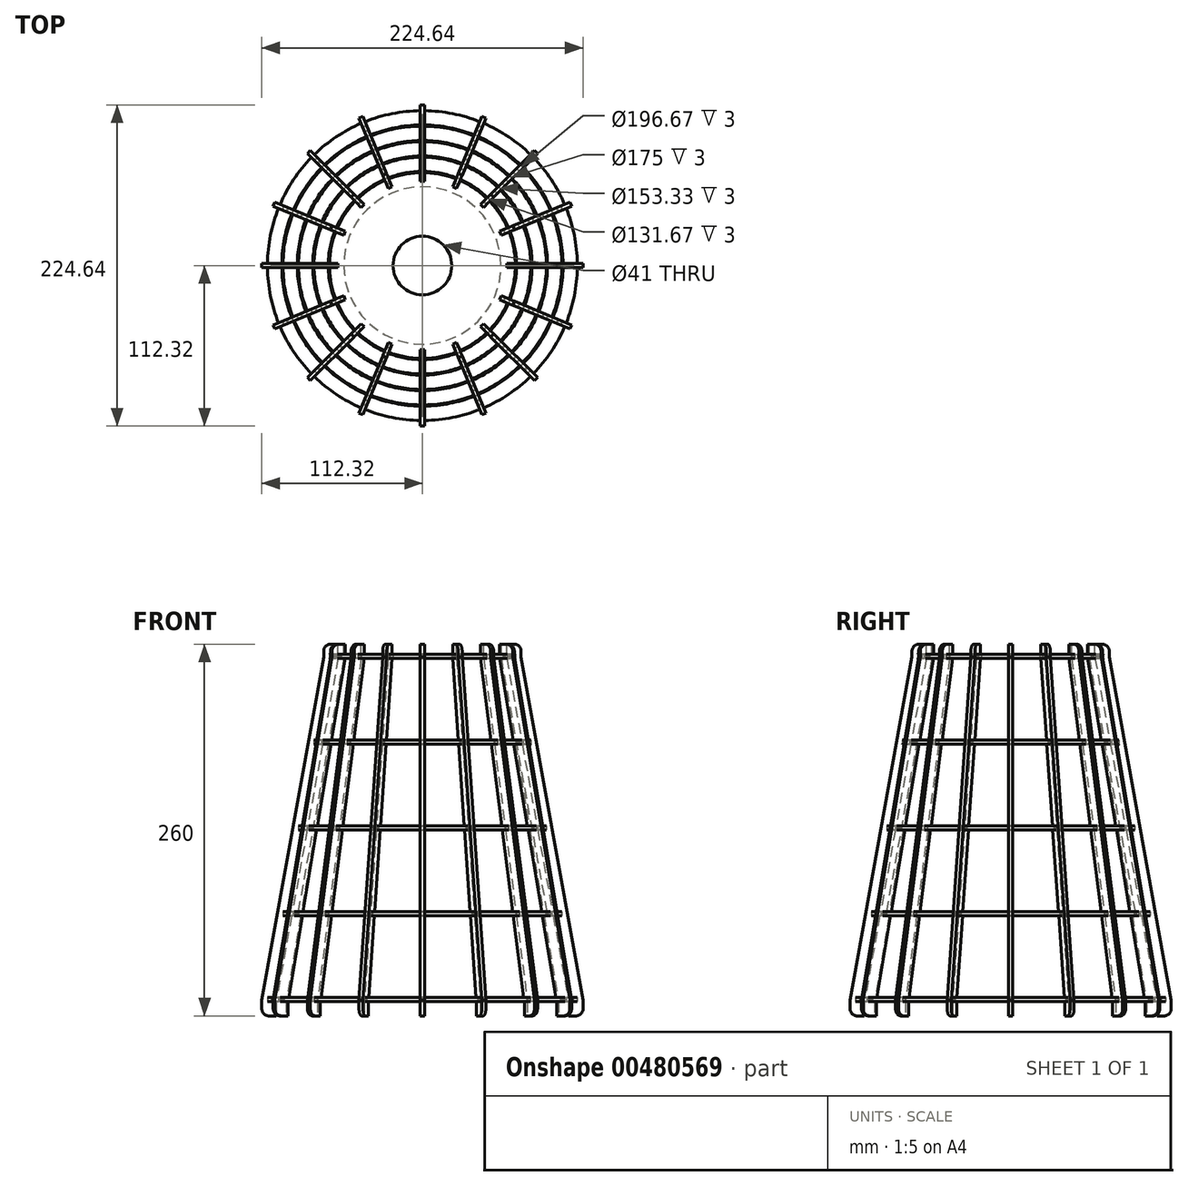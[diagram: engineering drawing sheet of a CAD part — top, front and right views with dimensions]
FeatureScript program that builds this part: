
annotation { "Feature Type Name" : "Feature", "Feature Type Description" : "" }
export const myFeature = defineFeature(function(context is Context, id is Id, definition is map)
    precondition{}
    {
        {
            var Q0;
            Q0=qCreatedBy(makeId("Top.planeOp"),FACE);
            cPlane(context, id + "F0", {"entities" : qUnion([Q0]), "cplaneType" : CPlaneType.OFFSET, "offset" : 60 * mm, "width" : 150 * mm, "height" : 150 * mm});
        }
        {
            var Q0;
            Q0=qCreatedBy(makeId("Top.planeOp"),FACE);
            cPlane(context, id + "F1", {"entities" : qUnion([Q0]), "cplaneType" : CPlaneType.OFFSET, "offset" : 60 * mm, "oppositeDirection" : true, "width" : 150 * mm, "height" : 150 * mm});
        }
        {
            var Q0;
            Q0=qCreatedBy(makeId("Top.planeOp"),FACE);
            cPlane(context, id + "F2", {"entities" : qUnion([Q0]), "cplaneType" : CPlaneType.OFFSET, "offset" : 120 * mm, "oppositeDirection" : true, "width" : 150 * mm, "height" : 150 * mm});
        }
        {
            var Q0;
            Q0=qCreatedBy(makeId("Top.planeOp"),FACE);
            cPlane(context, id + "F3", {"entities" : qUnion([Q0]), "cplaneType" : CPlaneType.OFFSET, "offset" : 180 * mm, "oppositeDirection" : true, "width" : 150 * mm, "height" : 150 * mm});
        }
        {
            var Q0;
            Q0=qCreatedBy(makeId("Front.planeOp"),FACE);
            var sketch = newSketch(context, id + "F4", { "sketchPlane" : qUnion([Q0])});
            skLineSegment(sketch, "E0", {"start": v(-55, 60) * mm, "end": v(-87.5, -120) * mm});
            skLineSegment(sketch, "E1", {"start": v(0, 0) * mm, "end": v(-65.83, 0) * mm});
            skLineSegment(sketch, "E2", {"start": v(0, -60) * mm, "end": v(-76.67, -60) * mm});
            skLineSegment(sketch, "E3", {"start": v(0, -180) * mm, "end": v(-98.33, -180) * mm});
            skLineSegment(sketch, "E4", {"start": v(-87.5, -120) * mm, "end": v(0, -120) * mm});
            skLineSegment(sketch, "E5", {"start": v(-55, 60) * mm, "end": v(0, 60) * mm});
            skLineSegment(sketch, "E6", {"start": v(0, 60) * mm, "end": v(0, -120) * mm});
            skSolve(sketch);
        }
        {
            var Q0;
            {var subQ2=sQuery(id+"F4.wireOp",EDGE,"E1");Q0=makeQuery(id+"F4.imprint","IMPRINT",FACE,{"disambiguationData":[TD([[makeQuery(id+"F4.imprint","IMPRINT",EDGE,{"derivedFrom":subQ2}),-1.0]])]});}
            var Q1;
            {var subQ0=sQuery(id+"F4.wireOp",EDGE,"E1");Q1=makeQuery(id+"F4.imprint","IMPRINT",FACE,{"disambiguationData":[TD([[makeQuery(id+"F4.imprint","IMPRINT",EDGE,{"derivedFrom":subQ0}),1.0]])]});}
            var Q2;
            {var subQ2=sQuery(id+"F4.wireOp",EDGE,"E2");Q2=makeQuery(id+"F4.imprint","IMPRINT",FACE,{"disambiguationData":[TD([[makeQuery(id+"F4.imprint","IMPRINT",EDGE,{"derivedFrom":subQ2}),1.0]])]});}
            var Q3;
            Q3=sQuery(id+"F4.wireOp",EDGE,"E6");
            revolve(context, id + "F5", {"entities" : qUnion([Q0, Q1, Q2]), "axis" : qUnion([Q3]), "revolveType" : RevolveType.FULL});
        }
        {
            var Q0;
            Q0=qCreatedBy(id+"F0.planeOp",FACE);
            var sketch = newSketch(context, id + "F6", { "sketchPlane" : qUnion([Q0])});
            skCircle(sketch, "E7", {"center": v(0, 0) * mm, "radius": 20.5 * mm});
            skArc(sketch, "E8", {"start": v(-64.98, -1.4) * mm, "mid": v(-63.75, -12.68) * mm, "end": v(-60.57, -23.58) * mm});
            skLineSegment(sketch, "E9", {"start": v(-64.98, 1.4) * mm, "end": v(-61.98, 1.4) * mm});
            skLineSegment(sketch, "E10", {"start": v(-61.98, 1.4) * mm, "end": v(-61.98, -1.4) * mm});
            skLineSegment(sketch, "E11", {"start": v(-61.98, -1.4) * mm, "end": v(-64.98, -1.4) * mm});
            skLineSegment(sketch, "E12.1.0", {"start": v(-60.57, -23.58) * mm, "end": v(-57.8, -22.43) * mm});
            skLineSegment(sketch, "E12.1.1", {"start": v(-57.8, -22.43) * mm, "end": v(-56.73, -25.01) * mm});
            skLineSegment(sketch, "E12.1.2", {"start": v(-56.73, -25.01) * mm, "end": v(-59.5, -26.16) * mm});
            skLineSegment(sketch, "E12.2.0", {"start": v(-46.94, -44.96) * mm, "end": v(-44.82, -42.84) * mm});
            skLineSegment(sketch, "E12.2.1", {"start": v(-44.82, -42.84) * mm, "end": v(-42.84, -44.82) * mm});
            skLineSegment(sketch, "E12.2.2", {"start": v(-42.84, -44.82) * mm, "end": v(-44.96, -46.94) * mm});
            skLineSegment(sketch, "E12.3.0", {"start": v(-26.16, -59.5) * mm, "end": v(-25.01, -56.73) * mm});
            skLineSegment(sketch, "E12.3.1", {"start": v(-25.01, -56.73) * mm, "end": v(-22.43, -57.8) * mm});
            skLineSegment(sketch, "E12.3.2", {"start": v(-22.43, -57.8) * mm, "end": v(-23.58, -60.57) * mm});
            skLineSegment(sketch, "E12.4.0", {"start": v(-1.4, -64.98) * mm, "end": v(-1.4, -61.98) * mm});
            skLineSegment(sketch, "E12.4.1", {"start": v(-1.4, -61.98) * mm, "end": v(1.4, -61.98) * mm});
            skLineSegment(sketch, "E12.4.2", {"start": v(1.4, -61.98) * mm, "end": v(1.4, -64.98) * mm});
            skLineSegment(sketch, "E12.5.0", {"start": v(23.58, -60.57) * mm, "end": v(22.43, -57.8) * mm});
            skLineSegment(sketch, "E12.5.1", {"start": v(22.43, -57.8) * mm, "end": v(25.01, -56.73) * mm});
            skLineSegment(sketch, "E12.5.2", {"start": v(25.01, -56.73) * mm, "end": v(26.16, -59.5) * mm});
            skLineSegment(sketch, "E12.6.0", {"start": v(44.96, -46.94) * mm, "end": v(42.84, -44.82) * mm});
            skLineSegment(sketch, "E12.6.1", {"start": v(42.84, -44.82) * mm, "end": v(44.82, -42.84) * mm});
            skLineSegment(sketch, "E12.6.2", {"start": v(44.82, -42.84) * mm, "end": v(46.94, -44.96) * mm});
            skLineSegment(sketch, "E12.7.0", {"start": v(59.5, -26.16) * mm, "end": v(56.73, -25.01) * mm});
            skLineSegment(sketch, "E12.7.1", {"start": v(56.73, -25.01) * mm, "end": v(57.8, -22.43) * mm});
            skLineSegment(sketch, "E12.7.2", {"start": v(57.8, -22.43) * mm, "end": v(60.57, -23.58) * mm});
            skLineSegment(sketch, "E12.8.0", {"start": v(64.98, -1.4) * mm, "end": v(61.98, -1.4) * mm});
            skLineSegment(sketch, "E12.8.1", {"start": v(61.98, -1.4) * mm, "end": v(61.98, 1.4) * mm});
            skLineSegment(sketch, "E12.8.2", {"start": v(61.98, 1.4) * mm, "end": v(64.98, 1.4) * mm});
            skLineSegment(sketch, "E12.9.0", {"start": v(60.57, 23.58) * mm, "end": v(57.8, 22.43) * mm});
            skLineSegment(sketch, "E12.9.1", {"start": v(57.8, 22.43) * mm, "end": v(56.73, 25.01) * mm});
            skLineSegment(sketch, "E12.9.2", {"start": v(56.73, 25.01) * mm, "end": v(59.5, 26.16) * mm});
            skLineSegment(sketch, "E12.10.0", {"start": v(46.94, 44.96) * mm, "end": v(44.82, 42.84) * mm});
            skLineSegment(sketch, "E12.10.1", {"start": v(44.82, 42.84) * mm, "end": v(42.84, 44.82) * mm});
            skLineSegment(sketch, "E12.10.2", {"start": v(42.84, 44.82) * mm, "end": v(44.96, 46.94) * mm});
            skLineSegment(sketch, "E12.11.0", {"start": v(26.16, 59.5) * mm, "end": v(25.01, 56.73) * mm});
            skLineSegment(sketch, "E12.11.1", {"start": v(25.01, 56.73) * mm, "end": v(22.43, 57.8) * mm});
            skLineSegment(sketch, "E12.11.2", {"start": v(22.43, 57.8) * mm, "end": v(23.58, 60.57) * mm});
            skLineSegment(sketch, "E12.12.0", {"start": v(1.4, 64.98) * mm, "end": v(1.4, 61.98) * mm});
            skLineSegment(sketch, "E12.12.1", {"start": v(1.4, 61.98) * mm, "end": v(-1.4, 61.98) * mm});
            skLineSegment(sketch, "E12.12.2", {"start": v(-1.4, 61.98) * mm, "end": v(-1.4, 64.98) * mm});
            skLineSegment(sketch, "E12.13.0", {"start": v(-23.58, 60.57) * mm, "end": v(-22.43, 57.8) * mm});
            skLineSegment(sketch, "E12.13.1", {"start": v(-22.43, 57.8) * mm, "end": v(-25.01, 56.73) * mm});
            skLineSegment(sketch, "E12.13.2", {"start": v(-25.01, 56.73) * mm, "end": v(-26.16, 59.5) * mm});
            skLineSegment(sketch, "E12.14.0", {"start": v(-44.96, 46.94) * mm, "end": v(-42.84, 44.82) * mm});
            skLineSegment(sketch, "E12.14.1", {"start": v(-42.84, 44.82) * mm, "end": v(-44.82, 42.84) * mm});
            skLineSegment(sketch, "E12.14.2", {"start": v(-44.82, 42.84) * mm, "end": v(-46.94, 44.96) * mm});
            skLineSegment(sketch, "E12.15.0", {"start": v(-59.5, 26.16) * mm, "end": v(-56.73, 25.01) * mm});
            skLineSegment(sketch, "E12.15.1", {"start": v(-56.73, 25.01) * mm, "end": v(-57.8, 22.43) * mm});
            skLineSegment(sketch, "E12.15.2", {"start": v(-57.8, 22.43) * mm, "end": v(-60.57, 23.58) * mm});
            skArc(sketch, "E13.trimOffspring", {"start": v(-60.57, 23.58) * mm, "mid": v(-63.75, 12.68) * mm, "end": v(-64.98, 1.4) * mm});
            skArc(sketch, "E14.trimOffspring", {"start": v(-46.94, 44.96) * mm, "mid": v(-54.05, 36.11) * mm, "end": v(-59.5, 26.16) * mm});
            skArc(sketch, "E15.trimOffspring", {"start": v(-26.16, 59.5) * mm, "mid": v(-36.11, 54.05) * mm, "end": v(-44.96, 46.94) * mm});
            skArc(sketch, "E16.trimOffspring", {"start": v(-1.4, 64.98) * mm, "mid": v(-12.68, 63.75) * mm, "end": v(-23.58, 60.57) * mm});
            skArc(sketch, "E17.trimOffspring", {"start": v(23.58, 60.57) * mm, "mid": v(12.68, 63.75) * mm, "end": v(1.4, 64.98) * mm});
            skArc(sketch, "E18.trimOffspring", {"start": v(44.96, 46.94) * mm, "mid": v(36.11, 54.05) * mm, "end": v(26.16, 59.5) * mm});
            skArc(sketch, "E19.trimOffspring", {"start": v(59.5, 26.16) * mm, "mid": v(54.05, 36.11) * mm, "end": v(46.94, 44.96) * mm});
            skArc(sketch, "E20.trimOffspring", {"start": v(64.98, 1.4) * mm, "mid": v(63.75, 12.68) * mm, "end": v(60.57, 23.58) * mm});
            skArc(sketch, "E21.trimOffspring", {"start": v(60.57, -23.58) * mm, "mid": v(63.75, -12.68) * mm, "end": v(64.98, -1.4) * mm});
            skArc(sketch, "E22.trimOffspring", {"start": v(46.94, -44.96) * mm, "mid": v(54.05, -36.11) * mm, "end": v(59.5, -26.16) * mm});
            skArc(sketch, "E23.trimOffspring", {"start": v(26.16, -59.5) * mm, "mid": v(36.11, -54.05) * mm, "end": v(44.96, -46.94) * mm});
            skArc(sketch, "E24.trimOffspring", {"start": v(1.4, -64.98) * mm, "mid": v(12.68, -63.75) * mm, "end": v(23.58, -60.57) * mm});
            skArc(sketch, "E25.trimOffspring", {"start": v(-23.58, -60.57) * mm, "mid": v(-12.68, -63.75) * mm, "end": v(-1.4, -64.98) * mm});
            skArc(sketch, "E26.trimOffspring", {"start": v(-44.96, -46.94) * mm, "mid": v(-36.11, -54.05) * mm, "end": v(-26.16, -59.5) * mm});
            skArc(sketch, "E27.trimOffspring", {"start": v(-59.5, -26.16) * mm, "mid": v(-54.05, -36.11) * mm, "end": v(-46.94, -44.96) * mm});
            skSolve(sketch);
        }
        {
            var Q0;
            Q0 = qSketchRegion(id + "F6", true);
            extrude(context, id + "F7", {"entities" : qUnion([Q0]), "depth" : 3 * mm});
        }
        {
            var Q0;
            Q0=qCreatedBy(makeId("Top.planeOp"),FACE);
            var sketch = newSketch(context, id + "F8", { "sketchPlane" : qUnion([Q0])});
            skCircle(sketch, "E28", {"center": v(0, 0) * mm, "radius": 65.83 * mm});
            skArc(sketch, "E29", {"start": v(-75.82, -1.4) * mm, "mid": v(-74.38, -14.8) * mm, "end": v(-70.58, -27.72) * mm});
            skLineSegment(sketch, "E30", {"start": v(-75.82, 1.4) * mm, "end": v(-72.82, 1.4) * mm});
            skLineSegment(sketch, "E31", {"start": v(-72.82, 1.4) * mm, "end": v(-72.82, -1.4) * mm});
            skLineSegment(sketch, "E32", {"start": v(-72.82, -1.4) * mm, "end": v(-75.82, -1.4) * mm});
            skLineSegment(sketch, "E33.1.0", {"start": v(-70.58, -27.72) * mm, "end": v(-67.81, -26.57) * mm});
            skLineSegment(sketch, "E33.1.1", {"start": v(-67.81, -26.57) * mm, "end": v(-66.74, -29.16) * mm});
            skLineSegment(sketch, "E33.1.2", {"start": v(-66.74, -29.16) * mm, "end": v(-69.51, -30.3) * mm});
            skLineSegment(sketch, "E33.2.0", {"start": v(-54.6, -52.62) * mm, "end": v(-52.48, -50.5) * mm});
            skLineSegment(sketch, "E33.2.1", {"start": v(-52.48, -50.5) * mm, "end": v(-50.5, -52.48) * mm});
            skLineSegment(sketch, "E33.2.2", {"start": v(-50.5, -52.48) * mm, "end": v(-52.62, -54.6) * mm});
            skLineSegment(sketch, "E33.3.0", {"start": v(-30.3, -69.51) * mm, "end": v(-29.16, -66.74) * mm});
            skLineSegment(sketch, "E33.3.1", {"start": v(-29.16, -66.74) * mm, "end": v(-26.57, -67.81) * mm});
            skLineSegment(sketch, "E33.3.2", {"start": v(-26.57, -67.81) * mm, "end": v(-27.72, -70.58) * mm});
            skLineSegment(sketch, "E33.4.0", {"start": v(-1.4, -75.82) * mm, "end": v(-1.4, -72.82) * mm});
            skLineSegment(sketch, "E33.4.1", {"start": v(-1.4, -72.82) * mm, "end": v(1.4, -72.82) * mm});
            skLineSegment(sketch, "E33.4.2", {"start": v(1.4, -72.82) * mm, "end": v(1.4, -75.82) * mm});
            skLineSegment(sketch, "E33.5.0", {"start": v(27.72, -70.58) * mm, "end": v(26.57, -67.81) * mm});
            skLineSegment(sketch, "E33.5.1", {"start": v(26.57, -67.81) * mm, "end": v(29.16, -66.74) * mm});
            skLineSegment(sketch, "E33.5.2", {"start": v(29.16, -66.74) * mm, "end": v(30.3, -69.51) * mm});
            skLineSegment(sketch, "E33.6.0", {"start": v(52.62, -54.6) * mm, "end": v(50.5, -52.48) * mm});
            skLineSegment(sketch, "E33.6.1", {"start": v(50.5, -52.48) * mm, "end": v(52.48, -50.5) * mm});
            skLineSegment(sketch, "E33.6.2", {"start": v(52.48, -50.5) * mm, "end": v(54.6, -52.62) * mm});
            skLineSegment(sketch, "E33.7.0", {"start": v(69.51, -30.3) * mm, "end": v(66.74, -29.16) * mm});
            skLineSegment(sketch, "E33.7.1", {"start": v(66.74, -29.16) * mm, "end": v(67.81, -26.57) * mm});
            skLineSegment(sketch, "E33.7.2", {"start": v(67.81, -26.57) * mm, "end": v(70.58, -27.72) * mm});
            skLineSegment(sketch, "E33.8.0", {"start": v(75.82, -1.4) * mm, "end": v(72.82, -1.4) * mm});
            skLineSegment(sketch, "E33.8.1", {"start": v(72.82, -1.4) * mm, "end": v(72.82, 1.4) * mm});
            skLineSegment(sketch, "E33.8.2", {"start": v(72.82, 1.4) * mm, "end": v(75.82, 1.4) * mm});
            skLineSegment(sketch, "E33.9.0", {"start": v(70.58, 27.72) * mm, "end": v(67.81, 26.57) * mm});
            skLineSegment(sketch, "E33.9.1", {"start": v(67.81, 26.57) * mm, "end": v(66.74, 29.16) * mm});
            skLineSegment(sketch, "E33.9.2", {"start": v(66.74, 29.16) * mm, "end": v(69.51, 30.3) * mm});
            skLineSegment(sketch, "E33.10.0", {"start": v(54.6, 52.62) * mm, "end": v(52.48, 50.5) * mm});
            skLineSegment(sketch, "E33.10.1", {"start": v(52.48, 50.5) * mm, "end": v(50.5, 52.48) * mm});
            skLineSegment(sketch, "E33.10.2", {"start": v(50.5, 52.48) * mm, "end": v(52.62, 54.6) * mm});
            skLineSegment(sketch, "E33.11.0", {"start": v(30.3, 69.51) * mm, "end": v(29.16, 66.74) * mm});
            skLineSegment(sketch, "E33.11.1", {"start": v(29.16, 66.74) * mm, "end": v(26.57, 67.81) * mm});
            skLineSegment(sketch, "E33.11.2", {"start": v(26.57, 67.81) * mm, "end": v(27.72, 70.58) * mm});
            skLineSegment(sketch, "E33.12.0", {"start": v(1.4, 75.82) * mm, "end": v(1.4, 72.82) * mm});
            skLineSegment(sketch, "E33.12.1", {"start": v(1.4, 72.82) * mm, "end": v(-1.4, 72.82) * mm});
            skLineSegment(sketch, "E33.12.2", {"start": v(-1.4, 72.82) * mm, "end": v(-1.4, 75.82) * mm});
            skLineSegment(sketch, "E33.13.0", {"start": v(-27.72, 70.58) * mm, "end": v(-26.57, 67.81) * mm});
            skLineSegment(sketch, "E33.13.1", {"start": v(-26.57, 67.81) * mm, "end": v(-29.16, 66.74) * mm});
            skLineSegment(sketch, "E33.13.2", {"start": v(-29.16, 66.74) * mm, "end": v(-30.3, 69.51) * mm});
            skLineSegment(sketch, "E33.14.0", {"start": v(-52.62, 54.6) * mm, "end": v(-50.5, 52.48) * mm});
            skLineSegment(sketch, "E33.14.1", {"start": v(-50.5, 52.48) * mm, "end": v(-52.48, 50.5) * mm});
            skLineSegment(sketch, "E33.14.2", {"start": v(-52.48, 50.5) * mm, "end": v(-54.6, 52.62) * mm});
            skLineSegment(sketch, "E33.15.0", {"start": v(-69.51, 30.3) * mm, "end": v(-66.74, 29.16) * mm});
            skLineSegment(sketch, "E33.15.1", {"start": v(-66.74, 29.16) * mm, "end": v(-67.81, 26.57) * mm});
            skLineSegment(sketch, "E33.15.2", {"start": v(-67.81, 26.57) * mm, "end": v(-70.58, 27.72) * mm});
            skArc(sketch, "E34.trimOffspring", {"start": v(-70.58, 27.72) * mm, "mid": v(-74.38, 14.8) * mm, "end": v(-75.82, 1.4) * mm});
            skArc(sketch, "E35.trimOffspring", {"start": v(-54.6, 52.62) * mm, "mid": v(-63.05, 42.13) * mm, "end": v(-69.51, 30.3) * mm});
            skArc(sketch, "E36.trimOffspring", {"start": v(-30.3, 69.51) * mm, "mid": v(-42.13, 63.05) * mm, "end": v(-52.62, 54.6) * mm});
            skArc(sketch, "E37.trimOffspring", {"start": v(-1.4, 75.82) * mm, "mid": v(-14.8, 74.38) * mm, "end": v(-27.72, 70.58) * mm});
            skArc(sketch, "E38.trimOffspring", {"start": v(27.72, 70.58) * mm, "mid": v(14.8, 74.38) * mm, "end": v(1.4, 75.82) * mm});
            skArc(sketch, "E39.trimOffspring", {"start": v(52.62, 54.6) * mm, "mid": v(42.13, 63.05) * mm, "end": v(30.3, 69.51) * mm});
            skArc(sketch, "E40.trimOffspring", {"start": v(69.51, 30.3) * mm, "mid": v(63.05, 42.13) * mm, "end": v(54.6, 52.62) * mm});
            skArc(sketch, "E41.trimOffspring", {"start": v(75.82, 1.4) * mm, "mid": v(74.38, 14.8) * mm, "end": v(70.58, 27.72) * mm});
            skArc(sketch, "E42.trimOffspring", {"start": v(70.58, -27.72) * mm, "mid": v(74.38, -14.8) * mm, "end": v(75.82, -1.4) * mm});
            skArc(sketch, "E43.trimOffspring", {"start": v(54.6, -52.62) * mm, "mid": v(63.05, -42.13) * mm, "end": v(69.51, -30.3) * mm});
            skArc(sketch, "E44.trimOffspring", {"start": v(30.3, -69.51) * mm, "mid": v(42.13, -63.05) * mm, "end": v(52.62, -54.6) * mm});
            skArc(sketch, "E45.trimOffspring", {"start": v(1.4, -75.82) * mm, "mid": v(14.8, -74.38) * mm, "end": v(27.72, -70.58) * mm});
            skArc(sketch, "E46.trimOffspring", {"start": v(-27.72, -70.58) * mm, "mid": v(-14.8, -74.38) * mm, "end": v(-1.4, -75.82) * mm});
            skArc(sketch, "E47.trimOffspring", {"start": v(-52.62, -54.6) * mm, "mid": v(-42.13, -63.05) * mm, "end": v(-30.3, -69.51) * mm});
            skArc(sketch, "E48.trimOffspring", {"start": v(-69.51, -30.3) * mm, "mid": v(-63.05, -42.13) * mm, "end": v(-54.6, -52.62) * mm});
            skSolve(sketch);
        }
        {
            var Q0;
            Q0 = qSketchRegion(id + "F8", true);
            extrude(context, id + "F9", {"entities" : qUnion([Q0]), "depth" : 3 * mm});
        }
        {
            var Q0;
            Q0=qCreatedBy(id+"F1.planeOp",FACE);
            var sketch = newSketch(context, id + "F10", { "sketchPlane" : qUnion([Q0])});
            skCircle(sketch, "E49", {"center": v(0, 0) * mm, "radius": 76.67 * mm});
            skArc(sketch, "E50", {"start": v(-86.66, -1.4) * mm, "mid": v(-85, -16.9) * mm, "end": v(-80.6, -31.87) * mm});
            skLineSegment(sketch, "E51", {"start": v(-86.67, 1.4) * mm, "end": v(-83.67, 1.4) * mm});
            skLineSegment(sketch, "E52", {"start": v(-83.67, 1.4) * mm, "end": v(-83.67, -1.4) * mm});
            skLineSegment(sketch, "E53", {"start": v(-83.67, -1.4) * mm, "end": v(-86.66, -1.4) * mm});
            skLineSegment(sketch, "E54.1.0", {"start": v(-80.6, -31.87) * mm, "end": v(-77.83, -30.72) * mm});
            skLineSegment(sketch, "E54.1.1", {"start": v(-77.83, -30.72) * mm, "end": v(-76.76, -33.31) * mm});
            skLineSegment(sketch, "E54.1.2", {"start": v(-76.76, -33.31) * mm, "end": v(-79.52, -34.46) * mm});
            skLineSegment(sketch, "E54.2.0", {"start": v(-62.27, -60.3) * mm, "end": v(-60.15, -58.17) * mm});
            skLineSegment(sketch, "E54.2.1", {"start": v(-60.15, -58.17) * mm, "end": v(-58.17, -60.15) * mm});
            skLineSegment(sketch, "E54.2.2", {"start": v(-58.17, -60.15) * mm, "end": v(-60.28, -62.26) * mm});
            skLineSegment(sketch, "E54.3.0", {"start": v(-34.46, -79.53) * mm, "end": v(-33.31, -76.76) * mm});
            skLineSegment(sketch, "E54.3.1", {"start": v(-33.31, -76.76) * mm, "end": v(-30.72, -77.83) * mm});
            skLineSegment(sketch, "E54.3.2", {"start": v(-30.72, -77.83) * mm, "end": v(-31.87, -80.6) * mm});
            skLineSegment(sketch, "E54.4.0", {"start": v(-1.4, -86.67) * mm, "end": v(-1.4, -83.67) * mm});
            skLineSegment(sketch, "E54.4.1", {"start": v(-1.4, -83.67) * mm, "end": v(1.4, -83.67) * mm});
            skLineSegment(sketch, "E54.4.2", {"start": v(1.4, -83.67) * mm, "end": v(1.4, -86.66) * mm});
            skLineSegment(sketch, "E54.5.0", {"start": v(31.87, -80.6) * mm, "end": v(30.72, -77.83) * mm});
            skLineSegment(sketch, "E54.5.1", {"start": v(30.72, -77.83) * mm, "end": v(33.31, -76.76) * mm});
            skLineSegment(sketch, "E54.5.2", {"start": v(33.31, -76.76) * mm, "end": v(34.46, -79.52) * mm});
            skLineSegment(sketch, "E54.6.0", {"start": v(60.3, -62.27) * mm, "end": v(58.17, -60.15) * mm});
            skLineSegment(sketch, "E54.6.1", {"start": v(58.17, -60.15) * mm, "end": v(60.15, -58.17) * mm});
            skLineSegment(sketch, "E54.6.2", {"start": v(60.15, -58.17) * mm, "end": v(62.26, -60.28) * mm});
            skLineSegment(sketch, "E54.7.0", {"start": v(79.53, -34.46) * mm, "end": v(76.76, -33.31) * mm});
            skLineSegment(sketch, "E54.7.1", {"start": v(76.76, -33.31) * mm, "end": v(77.83, -30.72) * mm});
            skLineSegment(sketch, "E54.7.2", {"start": v(77.83, -30.72) * mm, "end": v(80.6, -31.87) * mm});
            skLineSegment(sketch, "E54.8.0", {"start": v(86.67, -1.4) * mm, "end": v(83.67, -1.4) * mm});
            skLineSegment(sketch, "E54.8.1", {"start": v(83.67, -1.4) * mm, "end": v(83.67, 1.4) * mm});
            skLineSegment(sketch, "E54.8.2", {"start": v(83.67, 1.4) * mm, "end": v(86.66, 1.4) * mm});
            skLineSegment(sketch, "E54.9.0", {"start": v(80.6, 31.87) * mm, "end": v(77.83, 30.72) * mm});
            skLineSegment(sketch, "E54.9.1", {"start": v(77.83, 30.72) * mm, "end": v(76.76, 33.31) * mm});
            skLineSegment(sketch, "E54.9.2", {"start": v(76.76, 33.31) * mm, "end": v(79.52, 34.46) * mm});
            skLineSegment(sketch, "E54.10.0", {"start": v(62.27, 60.3) * mm, "end": v(60.15, 58.17) * mm});
            skLineSegment(sketch, "E54.10.1", {"start": v(60.15, 58.17) * mm, "end": v(58.17, 60.15) * mm});
            skLineSegment(sketch, "E54.10.2", {"start": v(58.17, 60.15) * mm, "end": v(60.28, 62.26) * mm});
            skLineSegment(sketch, "E54.11.0", {"start": v(34.46, 79.53) * mm, "end": v(33.31, 76.76) * mm});
            skLineSegment(sketch, "E54.11.1", {"start": v(33.31, 76.76) * mm, "end": v(30.72, 77.83) * mm});
            skLineSegment(sketch, "E54.11.2", {"start": v(30.72, 77.83) * mm, "end": v(31.87, 80.6) * mm});
            skLineSegment(sketch, "E54.12.0", {"start": v(1.4, 86.67) * mm, "end": v(1.4, 83.67) * mm});
            skLineSegment(sketch, "E54.12.1", {"start": v(1.4, 83.67) * mm, "end": v(-1.4, 83.67) * mm});
            skLineSegment(sketch, "E54.12.2", {"start": v(-1.4, 83.67) * mm, "end": v(-1.4, 86.66) * mm});
            skLineSegment(sketch, "E54.13.0", {"start": v(-31.87, 80.6) * mm, "end": v(-30.72, 77.83) * mm});
            skLineSegment(sketch, "E54.13.1", {"start": v(-30.72, 77.83) * mm, "end": v(-33.31, 76.76) * mm});
            skLineSegment(sketch, "E54.13.2", {"start": v(-33.31, 76.76) * mm, "end": v(-34.46, 79.52) * mm});
            skLineSegment(sketch, "E54.14.0", {"start": v(-60.3, 62.27) * mm, "end": v(-58.17, 60.15) * mm});
            skLineSegment(sketch, "E54.14.1", {"start": v(-58.17, 60.15) * mm, "end": v(-60.15, 58.17) * mm});
            skLineSegment(sketch, "E54.14.2", {"start": v(-60.15, 58.17) * mm, "end": v(-62.26, 60.28) * mm});
            skLineSegment(sketch, "E54.15.0", {"start": v(-79.53, 34.46) * mm, "end": v(-76.76, 33.31) * mm});
            skLineSegment(sketch, "E54.15.1", {"start": v(-76.76, 33.31) * mm, "end": v(-77.83, 30.72) * mm});
            skLineSegment(sketch, "E54.15.2", {"start": v(-77.83, 30.72) * mm, "end": v(-80.6, 31.87) * mm});
            skArc(sketch, "E55.trimOffspring", {"start": v(-80.6, 31.87) * mm, "mid": v(-85, 16.9) * mm, "end": v(-86.66, 1.4) * mm});
            skArc(sketch, "E56.trimOffspring", {"start": v(-62.26, 60.28) * mm, "mid": v(-72.06, 48.15) * mm, "end": v(-79.52, 34.46) * mm});
            skArc(sketch, "E57.trimOffspring", {"start": v(-34.46, 79.52) * mm, "mid": v(-48.15, 72.06) * mm, "end": v(-60.28, 62.26) * mm});
            skArc(sketch, "E58.trimOffspring", {"start": v(-1.4, 86.66) * mm, "mid": v(-16.9, 85) * mm, "end": v(-31.87, 80.6) * mm});
            skArc(sketch, "E59.trimOffspring", {"start": v(31.87, 80.6) * mm, "mid": v(16.9, 85) * mm, "end": v(1.4, 86.66) * mm});
            skArc(sketch, "E60.trimOffspring", {"start": v(60.28, 62.26) * mm, "mid": v(48.15, 72.06) * mm, "end": v(34.46, 79.52) * mm});
            skArc(sketch, "E61.trimOffspring", {"start": v(79.52, 34.46) * mm, "mid": v(72.06, 48.15) * mm, "end": v(62.26, 60.28) * mm});
            skArc(sketch, "E62.trimOffspring", {"start": v(86.66, 1.4) * mm, "mid": v(85, 16.9) * mm, "end": v(80.6, 31.87) * mm});
            skArc(sketch, "E63.trimOffspring", {"start": v(80.6, -31.87) * mm, "mid": v(85, -16.9) * mm, "end": v(86.66, -1.4) * mm});
            skArc(sketch, "E64.trimOffspring", {"start": v(62.26, -60.28) * mm, "mid": v(72.06, -48.15) * mm, "end": v(79.52, -34.46) * mm});
            skArc(sketch, "E65.trimOffspring", {"start": v(34.46, -79.52) * mm, "mid": v(48.15, -72.06) * mm, "end": v(60.28, -62.26) * mm});
            skArc(sketch, "E66.trimOffspring", {"start": v(1.4, -86.66) * mm, "mid": v(16.9, -85) * mm, "end": v(31.87, -80.6) * mm});
            skArc(sketch, "E67.trimOffspring", {"start": v(-31.87, -80.6) * mm, "mid": v(-16.9, -85) * mm, "end": v(-1.4, -86.66) * mm});
            skArc(sketch, "E68.trimOffspring", {"start": v(-60.28, -62.26) * mm, "mid": v(-48.15, -72.06) * mm, "end": v(-34.46, -79.52) * mm});
            skArc(sketch, "E69.trimOffspring", {"start": v(-79.52, -34.46) * mm, "mid": v(-72.06, -48.15) * mm, "end": v(-62.26, -60.28) * mm});
            skSolve(sketch);
        }
        {
            var Q0;
            Q0 = qSketchRegion(id + "F10", true);
            extrude(context, id + "F11", {"entities" : qUnion([Q0]), "depth" : 3 * mm});
        }
        {
            var Q0;
            Q0=qCreatedBy(id+"F2.planeOp",FACE);
            var sketch = newSketch(context, id + "F12", { "sketchPlane" : qUnion([Q0])});
            skCircle(sketch, "E70", {"center": v(0, 0) * mm, "radius": 87.5 * mm});
            skArc(sketch, "E71", {"start": v(-97.49, -1.4) * mm, "mid": v(-95.63, -19.02) * mm, "end": v(-90.6, -36.01) * mm});
            skLineSegment(sketch, "E72", {"start": v(-97.49, 1.4) * mm, "end": v(-94.49, 1.4) * mm});
            skLineSegment(sketch, "E73", {"start": v(-94.49, 1.4) * mm, "end": v(-94.49, -1.4) * mm});
            skLineSegment(sketch, "E74", {"start": v(-94.49, -1.4) * mm, "end": v(-97.49, -1.4) * mm});
            skLineSegment(sketch, "E75.1.0", {"start": v(-90.6, -36.01) * mm, "end": v(-87.83, -34.87) * mm});
            skLineSegment(sketch, "E75.1.1", {"start": v(-87.83, -34.87) * mm, "end": v(-86.76, -37.45) * mm});
            skLineSegment(sketch, "E75.1.2", {"start": v(-86.76, -37.45) * mm, "end": v(-89.53, -38.6) * mm});
            skLineSegment(sketch, "E75.2.0", {"start": v(-69.93, -67.95) * mm, "end": v(-67.8, -65.82) * mm});
            skLineSegment(sketch, "E75.2.1", {"start": v(-67.8, -65.82) * mm, "end": v(-65.82, -67.8) * mm});
            skLineSegment(sketch, "E75.2.2", {"start": v(-65.82, -67.8) * mm, "end": v(-67.95, -69.93) * mm});
            skLineSegment(sketch, "E75.3.0", {"start": v(-38.6, -89.53) * mm, "end": v(-37.45, -86.76) * mm});
            skLineSegment(sketch, "E75.3.1", {"start": v(-37.45, -86.76) * mm, "end": v(-34.87, -87.83) * mm});
            skLineSegment(sketch, "E75.3.2", {"start": v(-34.87, -87.83) * mm, "end": v(-36.01, -90.6) * mm});
            skLineSegment(sketch, "E75.4.0", {"start": v(-1.4, -97.49) * mm, "end": v(-1.4, -94.49) * mm});
            skLineSegment(sketch, "E75.4.1", {"start": v(-1.4, -94.49) * mm, "end": v(1.4, -94.49) * mm});
            skLineSegment(sketch, "E75.4.2", {"start": v(1.4, -94.49) * mm, "end": v(1.4, -97.49) * mm});
            skLineSegment(sketch, "E75.5.0", {"start": v(36.01, -90.6) * mm, "end": v(34.87, -87.83) * mm});
            skLineSegment(sketch, "E75.5.1", {"start": v(34.87, -87.83) * mm, "end": v(37.45, -86.76) * mm});
            skLineSegment(sketch, "E75.5.2", {"start": v(37.45, -86.76) * mm, "end": v(38.6, -89.53) * mm});
            skLineSegment(sketch, "E75.6.0", {"start": v(67.95, -69.93) * mm, "end": v(65.82, -67.8) * mm});
            skLineSegment(sketch, "E75.6.1", {"start": v(65.82, -67.8) * mm, "end": v(67.8, -65.82) * mm});
            skLineSegment(sketch, "E75.6.2", {"start": v(67.8, -65.82) * mm, "end": v(69.93, -67.95) * mm});
            skLineSegment(sketch, "E75.7.0", {"start": v(89.53, -38.6) * mm, "end": v(86.76, -37.45) * mm});
            skLineSegment(sketch, "E75.7.1", {"start": v(86.76, -37.45) * mm, "end": v(87.83, -34.87) * mm});
            skLineSegment(sketch, "E75.7.2", {"start": v(87.83, -34.87) * mm, "end": v(90.6, -36.01) * mm});
            skLineSegment(sketch, "E75.8.0", {"start": v(97.49, -1.4) * mm, "end": v(94.49, -1.4) * mm});
            skLineSegment(sketch, "E75.8.1", {"start": v(94.49, -1.4) * mm, "end": v(94.49, 1.4) * mm});
            skLineSegment(sketch, "E75.8.2", {"start": v(94.49, 1.4) * mm, "end": v(97.49, 1.4) * mm});
            skLineSegment(sketch, "E75.9.0", {"start": v(90.6, 36.01) * mm, "end": v(87.83, 34.87) * mm});
            skLineSegment(sketch, "E75.9.1", {"start": v(87.83, 34.87) * mm, "end": v(86.76, 37.45) * mm});
            skLineSegment(sketch, "E75.9.2", {"start": v(86.76, 37.45) * mm, "end": v(89.53, 38.6) * mm});
            skLineSegment(sketch, "E75.10.0", {"start": v(69.93, 67.95) * mm, "end": v(67.8, 65.82) * mm});
            skLineSegment(sketch, "E75.10.1", {"start": v(67.8, 65.82) * mm, "end": v(65.82, 67.8) * mm});
            skLineSegment(sketch, "E75.10.2", {"start": v(65.82, 67.8) * mm, "end": v(67.95, 69.93) * mm});
            skLineSegment(sketch, "E75.11.0", {"start": v(38.6, 89.53) * mm, "end": v(37.45, 86.76) * mm});
            skLineSegment(sketch, "E75.11.1", {"start": v(37.45, 86.76) * mm, "end": v(34.87, 87.83) * mm});
            skLineSegment(sketch, "E75.11.2", {"start": v(34.87, 87.83) * mm, "end": v(36.01, 90.6) * mm});
            skLineSegment(sketch, "E75.12.0", {"start": v(1.4, 97.49) * mm, "end": v(1.4, 94.49) * mm});
            skLineSegment(sketch, "E75.12.1", {"start": v(1.4, 94.49) * mm, "end": v(-1.4, 94.49) * mm});
            skLineSegment(sketch, "E75.12.2", {"start": v(-1.4, 94.49) * mm, "end": v(-1.4, 97.49) * mm});
            skLineSegment(sketch, "E75.13.0", {"start": v(-36.01, 90.6) * mm, "end": v(-34.87, 87.83) * mm});
            skLineSegment(sketch, "E75.13.1", {"start": v(-34.87, 87.83) * mm, "end": v(-37.45, 86.76) * mm});
            skLineSegment(sketch, "E75.13.2", {"start": v(-37.45, 86.76) * mm, "end": v(-38.6, 89.53) * mm});
            skLineSegment(sketch, "E75.14.0", {"start": v(-67.95, 69.93) * mm, "end": v(-65.82, 67.8) * mm});
            skLineSegment(sketch, "E75.14.1", {"start": v(-65.82, 67.8) * mm, "end": v(-67.8, 65.82) * mm});
            skLineSegment(sketch, "E75.14.2", {"start": v(-67.8, 65.82) * mm, "end": v(-69.93, 67.95) * mm});
            skLineSegment(sketch, "E75.15.0", {"start": v(-89.53, 38.6) * mm, "end": v(-86.76, 37.45) * mm});
            skLineSegment(sketch, "E75.15.1", {"start": v(-86.76, 37.45) * mm, "end": v(-87.83, 34.87) * mm});
            skLineSegment(sketch, "E75.15.2", {"start": v(-87.83, 34.87) * mm, "end": v(-90.6, 36.01) * mm});
            skArc(sketch, "E76.trimOffspring", {"start": v(-90.6, 36.01) * mm, "mid": v(-95.63, 19.02) * mm, "end": v(-97.49, 1.4) * mm});
            skArc(sketch, "E77.trimOffspring", {"start": v(-69.93, 67.95) * mm, "mid": v(-81.07, 54.17) * mm, "end": v(-89.53, 38.6) * mm});
            skArc(sketch, "E78.trimOffspring", {"start": v(-38.6, 89.53) * mm, "mid": v(-54.17, 81.07) * mm, "end": v(-67.95, 69.93) * mm});
            skArc(sketch, "E79.trimOffspring", {"start": v(-1.4, 97.49) * mm, "mid": v(-19.02, 95.63) * mm, "end": v(-36.01, 90.6) * mm});
            skArc(sketch, "E80.trimOffspring", {"start": v(36.01, 90.6) * mm, "mid": v(19.02, 95.63) * mm, "end": v(1.4, 97.49) * mm});
            skArc(sketch, "E81.trimOffspring", {"start": v(67.95, 69.93) * mm, "mid": v(54.17, 81.07) * mm, "end": v(38.6, 89.53) * mm});
            skArc(sketch, "E82.trimOffspring", {"start": v(89.53, 38.6) * mm, "mid": v(81.07, 54.17) * mm, "end": v(69.93, 67.95) * mm});
            skArc(sketch, "E83.trimOffspring", {"start": v(97.49, 1.4) * mm, "mid": v(95.63, 19.02) * mm, "end": v(90.6, 36.01) * mm});
            skArc(sketch, "E84.trimOffspring", {"start": v(90.6, -36.01) * mm, "mid": v(95.63, -19.02) * mm, "end": v(97.49, -1.4) * mm});
            skArc(sketch, "E85.trimOffspring", {"start": v(69.93, -67.95) * mm, "mid": v(81.07, -54.17) * mm, "end": v(89.53, -38.6) * mm});
            skArc(sketch, "E86.trimOffspring", {"start": v(38.6, -89.53) * mm, "mid": v(54.17, -81.07) * mm, "end": v(67.95, -69.93) * mm});
            skArc(sketch, "E87.trimOffspring", {"start": v(1.4, -97.49) * mm, "mid": v(19.02, -95.63) * mm, "end": v(36.01, -90.6) * mm});
            skArc(sketch, "E88.trimOffspring", {"start": v(-36.01, -90.6) * mm, "mid": v(-19.02, -95.63) * mm, "end": v(-1.4, -97.49) * mm});
            skArc(sketch, "E89.trimOffspring", {"start": v(-67.95, -69.93) * mm, "mid": v(-54.17, -81.07) * mm, "end": v(-38.6, -89.53) * mm});
            skArc(sketch, "E90.trimOffspring", {"start": v(-89.53, -38.6) * mm, "mid": v(-81.07, -54.17) * mm, "end": v(-69.93, -67.95) * mm});
            skSolve(sketch);
        }
        {
            var Q0;
            Q0 = qSketchRegion(id + "F12", true);
            extrude(context, id + "F13", {"entities" : qUnion([Q0]), "depth" : 3 * mm});
        }
        {
            var Q0;
            Q0=qCreatedBy(id+"F3.planeOp",FACE);
            var sketch = newSketch(context, id + "F14", { "sketchPlane" : qUnion([Q0])});
            skCircle(sketch, "E91", {"center": v(0, 0) * mm, "radius": 98.33 * mm});
            skArc(sketch, "E92", {"start": v(-108.32, -1.4) * mm, "mid": v(-106.25, -21.13) * mm, "end": v(-100.61, -40.16) * mm});
            skLineSegment(sketch, "E93", {"start": v(-108.32, 1.4) * mm, "end": v(-105.32, 1.4) * mm});
            skLineSegment(sketch, "E94", {"start": v(-105.32, 1.4) * mm, "end": v(-105.32, -1.4) * mm});
            skLineSegment(sketch, "E95", {"start": v(-105.32, -1.4) * mm, "end": v(-108.32, -1.4) * mm});
            skLineSegment(sketch, "E96.1.0", {"start": v(-100.61, -40.16) * mm, "end": v(-97.84, -39.01) * mm});
            skLineSegment(sketch, "E96.1.1", {"start": v(-96.77, -41.6) * mm, "end": v(-99.54, -42.75) * mm});
            skLineSegment(sketch, "E96.1.2", {"start": v(-97.84, -39.01) * mm, "end": v(-96.77, -41.6) * mm});
            skLineSegment(sketch, "E96.2.0", {"start": v(-77.59, -75.6) * mm, "end": v(-75.47, -73.49) * mm});
            skLineSegment(sketch, "E96.2.1", {"start": v(-73.49, -75.47) * mm, "end": v(-75.6, -77.59) * mm});
            skLineSegment(sketch, "E96.2.2", {"start": v(-75.47, -73.49) * mm, "end": v(-73.49, -75.47) * mm});
            skLineSegment(sketch, "E96.3.0", {"start": v(-42.75, -99.54) * mm, "end": v(-41.6, -96.77) * mm});
            skLineSegment(sketch, "E96.3.1", {"start": v(-39.01, -97.84) * mm, "end": v(-40.16, -100.61) * mm});
            skLineSegment(sketch, "E96.3.2", {"start": v(-41.6, -96.77) * mm, "end": v(-39.01, -97.84) * mm});
            skLineSegment(sketch, "E96.4.0", {"start": v(-1.4, -108.32) * mm, "end": v(-1.4, -105.32) * mm});
            skLineSegment(sketch, "E96.4.1", {"start": v(1.4, -105.32) * mm, "end": v(1.4, -108.32) * mm});
            skLineSegment(sketch, "E96.4.2", {"start": v(-1.4, -105.32) * mm, "end": v(1.4, -105.32) * mm});
            skLineSegment(sketch, "E96.5.0", {"start": v(40.16, -100.61) * mm, "end": v(39.01, -97.84) * mm});
            skLineSegment(sketch, "E96.5.1", {"start": v(41.6, -96.77) * mm, "end": v(42.75, -99.54) * mm});
            skLineSegment(sketch, "E96.5.2", {"start": v(39.01, -97.84) * mm, "end": v(41.6, -96.77) * mm});
            skLineSegment(sketch, "E96.6.0", {"start": v(75.6, -77.59) * mm, "end": v(73.49, -75.47) * mm});
            skLineSegment(sketch, "E96.6.1", {"start": v(75.47, -73.49) * mm, "end": v(77.59, -75.6) * mm});
            skLineSegment(sketch, "E96.6.2", {"start": v(73.49, -75.47) * mm, "end": v(75.47, -73.49) * mm});
            skLineSegment(sketch, "E96.7.0", {"start": v(99.54, -42.75) * mm, "end": v(96.77, -41.6) * mm});
            skLineSegment(sketch, "E96.7.1", {"start": v(97.84, -39.01) * mm, "end": v(100.61, -40.16) * mm});
            skLineSegment(sketch, "E96.7.2", {"start": v(96.77, -41.6) * mm, "end": v(97.84, -39.01) * mm});
            skLineSegment(sketch, "E96.8.0", {"start": v(108.32, -1.4) * mm, "end": v(105.32, -1.4) * mm});
            skLineSegment(sketch, "E96.8.1", {"start": v(105.32, 1.4) * mm, "end": v(108.32, 1.4) * mm});
            skLineSegment(sketch, "E96.8.2", {"start": v(105.32, -1.4) * mm, "end": v(105.32, 1.4) * mm});
            skLineSegment(sketch, "E96.9.0", {"start": v(100.61, 40.16) * mm, "end": v(97.84, 39.01) * mm});
            skLineSegment(sketch, "E96.9.1", {"start": v(96.77, 41.6) * mm, "end": v(99.54, 42.75) * mm});
            skLineSegment(sketch, "E96.9.2", {"start": v(97.84, 39.01) * mm, "end": v(96.77, 41.6) * mm});
            skLineSegment(sketch, "E96.10.0", {"start": v(77.59, 75.6) * mm, "end": v(75.47, 73.49) * mm});
            skLineSegment(sketch, "E96.10.1", {"start": v(73.49, 75.47) * mm, "end": v(75.6, 77.59) * mm});
            skLineSegment(sketch, "E96.10.2", {"start": v(75.47, 73.49) * mm, "end": v(73.49, 75.47) * mm});
            skLineSegment(sketch, "E96.11.0", {"start": v(42.75, 99.54) * mm, "end": v(41.6, 96.77) * mm});
            skLineSegment(sketch, "E96.11.1", {"start": v(39.01, 97.84) * mm, "end": v(40.16, 100.61) * mm});
            skLineSegment(sketch, "E96.11.2", {"start": v(41.6, 96.77) * mm, "end": v(39.01, 97.84) * mm});
            skLineSegment(sketch, "E96.12.0", {"start": v(1.4, 108.32) * mm, "end": v(1.4, 105.32) * mm});
            skLineSegment(sketch, "E96.12.1", {"start": v(-1.4, 105.32) * mm, "end": v(-1.4, 108.32) * mm});
            skLineSegment(sketch, "E96.12.2", {"start": v(1.4, 105.32) * mm, "end": v(-1.4, 105.32) * mm});
            skLineSegment(sketch, "E96.13.0", {"start": v(-40.16, 100.61) * mm, "end": v(-39.01, 97.84) * mm});
            skLineSegment(sketch, "E96.13.1", {"start": v(-41.6, 96.77) * mm, "end": v(-42.75, 99.54) * mm});
            skLineSegment(sketch, "E96.13.2", {"start": v(-39.01, 97.84) * mm, "end": v(-41.6, 96.77) * mm});
            skLineSegment(sketch, "E96.14.0", {"start": v(-75.6, 77.59) * mm, "end": v(-73.49, 75.47) * mm});
            skLineSegment(sketch, "E96.14.1", {"start": v(-75.47, 73.49) * mm, "end": v(-77.59, 75.6) * mm});
            skLineSegment(sketch, "E96.14.2", {"start": v(-73.49, 75.47) * mm, "end": v(-75.47, 73.49) * mm});
            skLineSegment(sketch, "E96.15.0", {"start": v(-99.54, 42.75) * mm, "end": v(-96.77, 41.6) * mm});
            skLineSegment(sketch, "E96.15.1", {"start": v(-97.84, 39.01) * mm, "end": v(-100.61, 40.16) * mm});
            skLineSegment(sketch, "E96.15.2", {"start": v(-96.77, 41.6) * mm, "end": v(-97.84, 39.01) * mm});
            skArc(sketch, "E97.trimOffspring", {"start": v(-100.61, 40.16) * mm, "mid": v(-106.25, 21.13) * mm, "end": v(-108.32, 1.4) * mm});
            skArc(sketch, "E98.trimOffspring", {"start": v(-77.59, 75.6) * mm, "mid": v(-90.08, 60.19) * mm, "end": v(-99.54, 42.75) * mm});
            skArc(sketch, "E99.trimOffspring", {"start": v(-42.75, 99.54) * mm, "mid": v(-60.19, 90.08) * mm, "end": v(-75.6, 77.59) * mm});
            skArc(sketch, "E100.trimOffspring", {"start": v(-1.4, 108.32) * mm, "mid": v(-21.13, 106.25) * mm, "end": v(-40.16, 100.61) * mm});
            skArc(sketch, "E101.trimOffspring", {"start": v(40.16, 100.61) * mm, "mid": v(21.13, 106.25) * mm, "end": v(1.4, 108.32) * mm});
            skArc(sketch, "E102.trimOffspring", {"start": v(75.6, 77.59) * mm, "mid": v(60.19, 90.08) * mm, "end": v(42.75, 99.54) * mm});
            skArc(sketch, "E103.trimOffspring", {"start": v(99.54, 42.75) * mm, "mid": v(90.08, 60.19) * mm, "end": v(77.59, 75.6) * mm});
            skArc(sketch, "E104.trimOffspring", {"start": v(108.32, 1.4) * mm, "mid": v(106.25, 21.13) * mm, "end": v(100.61, 40.16) * mm});
            skArc(sketch, "E105.trimOffspring", {"start": v(100.61, -40.16) * mm, "mid": v(106.25, -21.13) * mm, "end": v(108.32, -1.4) * mm});
            skArc(sketch, "E106.trimOffspring", {"start": v(77.59, -75.6) * mm, "mid": v(90.08, -60.19) * mm, "end": v(99.54, -42.75) * mm});
            skArc(sketch, "E107.trimOffspring", {"start": v(42.75, -99.54) * mm, "mid": v(60.19, -90.08) * mm, "end": v(75.6, -77.59) * mm});
            skArc(sketch, "E108.trimOffspring", {"start": v(1.4, -108.32) * mm, "mid": v(21.13, -106.25) * mm, "end": v(40.16, -100.61) * mm});
            skArc(sketch, "E109.trimOffspring", {"start": v(-40.16, -100.61) * mm, "mid": v(-21.13, -106.25) * mm, "end": v(-1.4, -108.32) * mm});
            skArc(sketch, "E110.trimOffspring", {"start": v(-75.6, -77.59) * mm, "mid": v(-60.19, -90.08) * mm, "end": v(-42.75, -99.54) * mm});
            skArc(sketch, "E111.trimOffspring", {"start": v(-99.54, -42.75) * mm, "mid": v(-90.08, -60.19) * mm, "end": v(-77.59, -75.6) * mm});
            skSolve(sketch);
        }
        {
            var Q0;
            Q0 = qSketchRegion(id + "F14", true);
            extrude(context, id + "F15", {"entities" : qUnion([Q0]), "depth" : 3 * mm});
        }
        {
            var Q0;
            Q0=qCreatedBy(makeId("Front.planeOp"),FACE);
            var sketch = newSketch(context, id + "F16", { "sketchPlane" : qUnion([Q0])});
            skLineSegment(sketch, "E112", {"start": v(-58.98, 60) * mm, "end": v(-69.31, 2.8) * mm});
            skLineSegment(sketch, "E113", {"start": v(-58.98, 62.8) * mm, "end": v(-58.98, 70) * mm});
            skLineSegment(sketch, "E114", {"start": v(-58.98, 70) * mm, "end": v(-63.98, 70) * mm});
            skLineSegment(sketch, "E115", {"start": v(-68.98, 65) * mm, "end": v(-68.98, 60.9) * mm});
            skLineSegment(sketch, "E116", {"start": v(-68.98, 60.9) * mm, "end": v(-112.32, -179.1) * mm});
            skPoint(sketch, "E117.visualSharp", {"position": v(-68.98, 70) * mm});
            skArc(sketch, "E117.filletArc", {"start": v(-63.98, 70) * mm, "mid": v(-67.52, 68.54) * mm, "end": v(-68.99, 65) * mm});
            skLineSegment(sketch, "E118", {"start": v(-102.32, -180) * mm, "end": v(-102.32, -190) * mm});
            skLineSegment(sketch, "E119", {"start": v(-102.32, -190) * mm, "end": v(-107.32, -190) * mm});
            skLineSegment(sketch, "E120", {"start": v(-112.32, -185) * mm, "end": v(-112.32, -179.1) * mm});
            skPoint(sketch, "E121.visualSharp", {"position": v(-112.32, -190) * mm});
            skArc(sketch, "E121.filletArc", {"start": v(-112.32, -185) * mm, "mid": v(-110.85, -188.54) * mm, "end": v(-107.32, -190) * mm});
            skLineSegment(sketch, "E122", {"start": v(-58.98, 60) * mm, "end": v(-61.98, 60) * mm});
            skLineSegment(sketch, "E123", {"start": v(-61.98, 60) * mm, "end": v(-61.98, 62.8) * mm});
            skLineSegment(sketch, "E124", {"start": v(-61.98, 62.8) * mm, "end": v(-58.98, 62.8) * mm});
            skLineSegment(sketch, "E125", {"start": v(-69.82, 0) * mm, "end": v(-72.82, 0) * mm});
            skLineSegment(sketch, "E126", {"start": v(-72.82, 0) * mm, "end": v(-72.82, 2.8) * mm});
            skLineSegment(sketch, "E127", {"start": v(-72.82, 2.8) * mm, "end": v(-69.31, 2.8) * mm});
            skLineSegment(sketch, "E128.trimOffspring", {"start": v(-69.82, 0) * mm, "end": v(-80.15, -57.2) * mm});
            skLineSegment(sketch, "E129", {"start": v(-80.65, -60) * mm, "end": v(-83.65, -60) * mm});
            skLineSegment(sketch, "E130", {"start": v(-83.65, -60) * mm, "end": v(-83.65, -57.2) * mm});
            skLineSegment(sketch, "E131", {"start": v(-83.65, -57.2) * mm, "end": v(-80.15, -57.2) * mm});
            skLineSegment(sketch, "E132.trimOffspring", {"start": v(-80.65, -60) * mm, "end": v(-90.98, -117.2) * mm});
            skLineSegment(sketch, "E133", {"start": v(-91.48, -120) * mm, "end": v(-94.48, -120) * mm});
            skLineSegment(sketch, "E134", {"start": v(-94.48, -120) * mm, "end": v(-94.48, -117.2) * mm});
            skLineSegment(sketch, "E135", {"start": v(-94.48, -117.2) * mm, "end": v(-90.98, -117.2) * mm});
            skLineSegment(sketch, "E136.trimOffspring", {"start": v(-91.48, -120) * mm, "end": v(-101.81, -177.2) * mm});
            skLineSegment(sketch, "E137", {"start": v(-102.32, -180) * mm, "end": v(-105.32, -180) * mm});
            skLineSegment(sketch, "E138", {"start": v(-105.32, -180) * mm, "end": v(-105.32, -177.2) * mm});
            skLineSegment(sketch, "E139", {"start": v(-105.32, -177.2) * mm, "end": v(-101.81, -177.2) * mm});
            skSolve(sketch);
        }
        {
            var Q0;
            Q0 = qSketchRegion(id + "F16", true);
            extrude(context, id + "F17", {"entities" : qUnion([Q0]), "endBound" : BoundingType.SYMMETRIC, "depth" : 3 * mm});
        }
        {
            var Q0;
            Q0=makeQuery(id+"F17.opExtrude","SWEPT_BODY",BODY,{"disambiguationData":[OSD([sQuery(id+"F16.wireOp",EDGE,"E112"),sQuery(id+"F16.wireOp",EDGE,"E113"),sQuery(id+"F16.wireOp",EDGE,"E114"),sQuery(id+"F16.wireOp",EDGE,"E115"),sQuery(id+"F16.wireOp",EDGE,"E116"),sQuery(id+"F16.wireOp",EDGE,"E117.filletArc"),sQuery(id+"F16.wireOp",EDGE,"E118"),sQuery(id+"F16.wireOp",EDGE,"E119"),sQuery(id+"F16.wireOp",EDGE,"E120"),sQuery(id+"F16.wireOp",EDGE,"E121.filletArc")])]});
            var Q1;
            Q1=sQuery(id+"F4.wireOp",EDGE,"E6");
            circularPattern(context, id + "F18", {"entities" : qUnion([Q0]), "axis" : qUnion([Q1]), "angle" : 360 * degree, "instanceCount" : 16, "equalSpace" : true});
        }
    });
